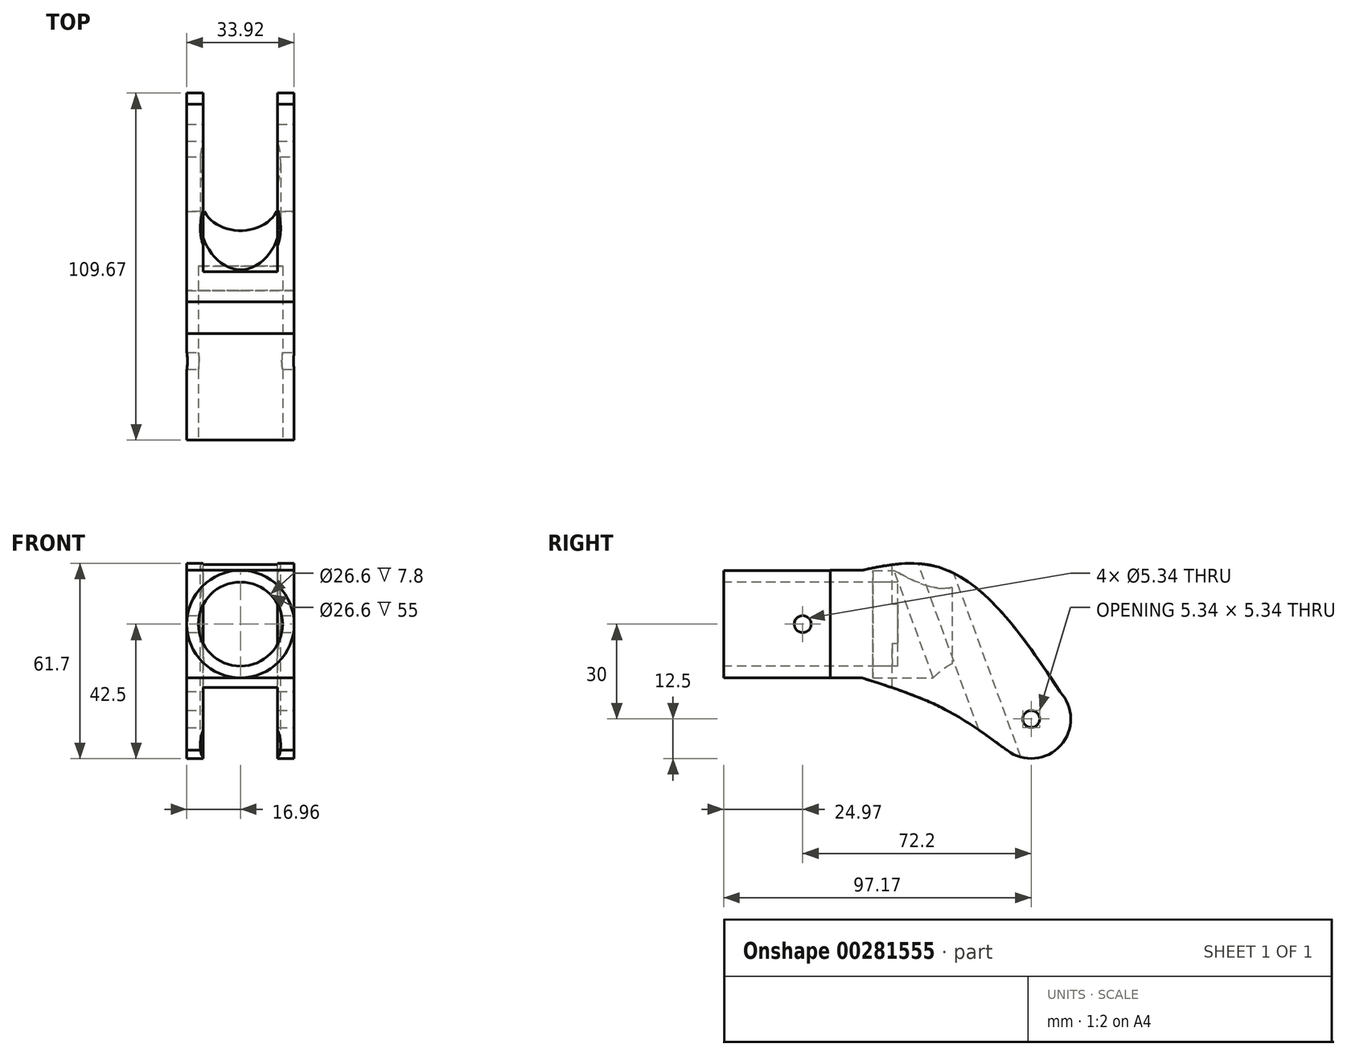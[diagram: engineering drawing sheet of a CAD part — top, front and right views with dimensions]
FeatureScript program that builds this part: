
annotation { "Feature Type Name" : "Feature", "Feature Type Description" : "" }
export const myFeature = defineFeature(function(context is Context, id is Id, definition is map)
    precondition{}
    {
        {
            var Q0;
            Q0=qCreatedBy(makeId("Front.planeOp"),FACE);
            var sketch = newSketch(context, id + "F0", { "sketchPlane" : qUnion([Q0])});
            skCircle(sketch, "E0", {"center": v(-16.96, 0) * mm, "radius": 16.96 * mm});
            skSolve(sketch);
        }
        {
            var Q0;
            Q0 = qSketchRegion(id + "F0", true);
            var Q1;
            Q1=sQuery(id+"F0.wireOp",EDGE,"E0");
            extrude(context, id + "F1", {"entities" : qUnion([Q0]), "surfaceEntities" : qUnion([Q1]), "depth" : 72.2 * mm});
        }
        {
            var Q0;
            Q0=qCreatedBy(makeId("Right.planeOp"),FACE);
            var sketch = newSketch(context, id + "F2", { "sketchPlane" : qUnion([Q0])});
            skLineSegment(sketch, "E1.bottom", {"start": v(-38.53, 17) * mm, "end": v(-28.53, 17) * mm});
            skLineSegment(sketch, "E1.top", {"start": v(-38.53, -17) * mm, "end": v(-28.53, -17) * mm});
            skLineSegment(sketch, "E1.left", {"start": v(-38.53, 17) * mm, "end": v(-38.53, -17) * mm});
            skLineSegment(sketch, "E1.right", {"start": v(-28.53, 17) * mm, "end": v(-28.53, -17) * mm});
            skCircle(sketch, "E2", {"center": v(24.97, -30) * mm, "radius": 12.5 * mm});
            skFitSpline(sketch, "E3", {"points": [v(17.68, -40.15) * mm, v(-28.53, -17) * mm], "startDerivative": vector(-53.03, 39.46) * mm, "endDerivative": vector(-69.4, 21.9) * mm});
            skFitSpline(sketch, "E4", {"points": [v(-28.53, 17) * mm, v(0, 16.35) * mm, v(34, -21.35) * mm], "startDerivative": vector(90.9, 21.22) * mm, "endDerivative": vector(72.14, -112.07) * mm});
            skSolve(sketch);
        }
        {
            var Q0;
            Q0 = qSketchRegion(id + "F2", true);
            extrude(context, id + "F3", {"entities" : qUnion([Q0]), "operationType" : NewBodyOperationType.ADD, "oppositeDirection" : true, "depth" : 33.92 * mm});
        }
        {
            var Q0;
            Q0=qCreatedBy(makeId("Top.planeOp"),FACE);
            var sketch = newSketch(context, id + "F4", { "sketchPlane" : qUnion([Q0])});
            skLineSegment(sketch, "E5.bottom", {"start": v(-28.71, 52.1) * mm, "end": v(-5.21, 52.1) * mm});
            skLineSegment(sketch, "E5.top", {"start": v(-28.71, -19) * mm, "end": v(-5.2, -19) * mm});
            skLineSegment(sketch, "E5.left", {"start": v(-28.71, 52.1) * mm, "end": v(-28.71, -19.01) * mm});
            skLineSegment(sketch, "E5.right", {"start": v(-5.21, 52.1) * mm, "end": v(-5.2, -19) * mm});
            skSolve(sketch);
        }
        {
            var Q0;
            Q0 = qSketchRegion(id + "F4", true);
            extrude(context, id + "F5", {"entities" : qUnion([Q0]), "operationType" : NewBodyOperationType.REMOVE, "endBound" : BoundingType.SYMMETRIC, "oppositeDirection" : true, "depth" : 100 * mm});
        }
        {
            var Q0;
            Q0 = qSketchRegion(id + "F0", true);
            extrude(context, id + "F6", {"entities" : qUnion([Q0]), "depth" : 25 * mm});
        }
        {
            var Q0;
            Q0=makeQuery(id+"F5.boolean.opBoolean","INTERSECT",EDGE,{"derivedFrom":[makeQuery(id+"F3.opExtrude","SWEPT_FACE",FACE,{"disambiguationData":[OSD([sQuery(id+"F2.wireOp",EDGE,"E4")])]}),makeQuery(id+"F5.opExtrude","SWEPT_FACE",FACE,{"disambiguationData":[OSD([sQuery(id+"F4.wireOp",EDGE,"E5.top")])]})]});
            cPlane(context, id + "F7", {"entities" : qUnion([Q0]), "cplaneType" : CPlaneType.LINE_ANGLE, "offset" : 25 * mm, "angle" : 110 * degree, "width" : 150 * mm, "height" : 150 * mm});
        }
        {
            var Q0;
            Q0=qCreatedBy(id+"F7.planeOp",FACE);
            var sketch = newSketch(context, id + "F8", { "sketchPlane" : qUnion([Q0])});
            skCircle(sketch, "E6", {"center": v(-16.96, 1.24) * mm, "radius": 12.68 * mm});
            skLineSegment(sketch, "E7", {"start": v(-16.96, 29.11) * mm, "end": v(-16.96, -4.78) * mm, "construction": true});
            skSolve(sketch);
        }
        {
            var Q0;
            Q0 = qSketchRegion(id + "F8", true);
            extrude(context, id + "F9", {"entities" : qUnion([Q0]), "operationType" : NewBodyOperationType.REMOVE, "endBound" : BoundingType.THROUGH_ALL, "oppositeDirection" : true, "depth" : 25 * mm});
        }
        {
            var Q0;
            {var subQ0=sQuery(id+"F2.wireOp",EDGE,"E1.right");Q0=makeQuery(id+"F2.imprint","IMPRINT",FACE,{"disambiguationData":[TD([[makeQuery(id+"F2.imprint","IMPRINT",EDGE,{"derivedFrom":subQ0}),1.0]])]});}
            var sketch = newSketch(context, id + "F10", { "sketchPlane" : qUnion([Q0])});
            skCircle(sketch, "E8", {"center": v(24.97, -30) * mm, "radius": 2.67 * mm});
            skSolve(sketch);
        }
        {
            var Q0;
            Q0=makeQuery(id+"F10.imprint","IMPRINT",FACE,{"disambiguationData":[TD([[makeQuery(id+"F10.imprint","IMPRINT",EDGE,{"derivedFrom":sQuery(id+"F10.wireOp",EDGE,"E8")}),1.0]])]});
            var Q1;
            Q1=sQuery(id+"F10.wireOp",EDGE,"E8");
            extrude(context, id + "F11", {"entities" : qUnion([Q0]), "operationType" : NewBodyOperationType.REMOVE, "surfaceEntities" : qUnion([Q1]), "endBound" : BoundingType.THROUGH_ALL, "oppositeDirection" : true, "depth" : 25 * mm});
        }
        {
            var Q0;
            {var subQ0=sQuery(id+"F2.wireOp",EDGE,"E1.right");Q0=makeQuery(id+"F2.imprint","IMPRINT",FACE,{"disambiguationData":[TD([[makeQuery(id+"F2.imprint","IMPRINT",EDGE,{"derivedFrom":subQ0}),1.0]])]});}
            var sketch = newSketch(context, id + "F12", { "sketchPlane" : qUnion([Q0])});
            skCircle(sketch, "E9", {"center": v(-47.23, 0) * mm, "radius": 2.67 * mm});
            skSolve(sketch);
        }
        {
            var Q0;
            Q0=makeQuery(id+"F12.imprint","IMPRINT",FACE,{"disambiguationData":[TD([[makeQuery(id+"F12.imprint","IMPRINT",EDGE,{"derivedFrom":sQuery(id+"F12.wireOp",EDGE,"E9")}),1.0]])]});
            var Q1;
            Q1=sQuery(id+"F12.wireOp",EDGE,"E9");
            extrude(context, id + "F13", {"entities" : qUnion([Q0]), "operationType" : NewBodyOperationType.REMOVE, "surfaceEntities" : qUnion([Q1]), "endBound" : BoundingType.THROUGH_ALL, "oppositeDirection" : true, "depth" : 25 * mm});
        }
        {
            var Q0;
            Q0=makeQuery(id+"F1.opExtrude","CAP_FACE",FACE,{"disambiguationData":[OSD([sQuery(id+"F0.wireOp",EDGE,"E0")])],"isStart":false});
            var sketch = newSketch(context, id + "F14", { "sketchPlane" : qUnion([Q0])});
            skCircle(sketch, "E10", {"center": v(-16.96, 0) * mm, "radius": 13.3 * mm});
            skSolve(sketch);
        }
        {
            var Q0;
            Q0=makeQuery(id+"F14.imprint","IMPRINT",FACE,{"disambiguationData":[TD([[makeQuery(id+"F14.imprint","IMPRINT",EDGE,{"derivedFrom":sQuery(id+"F14.wireOp",EDGE,"E10")}),1.0]])]});
            extrude(context, id + "F15", {"entities" : qUnion([Q0]), "operationType" : NewBodyOperationType.REMOVE, "oppositeDirection" : true, "depth" : 55 * mm});
        }
    });
